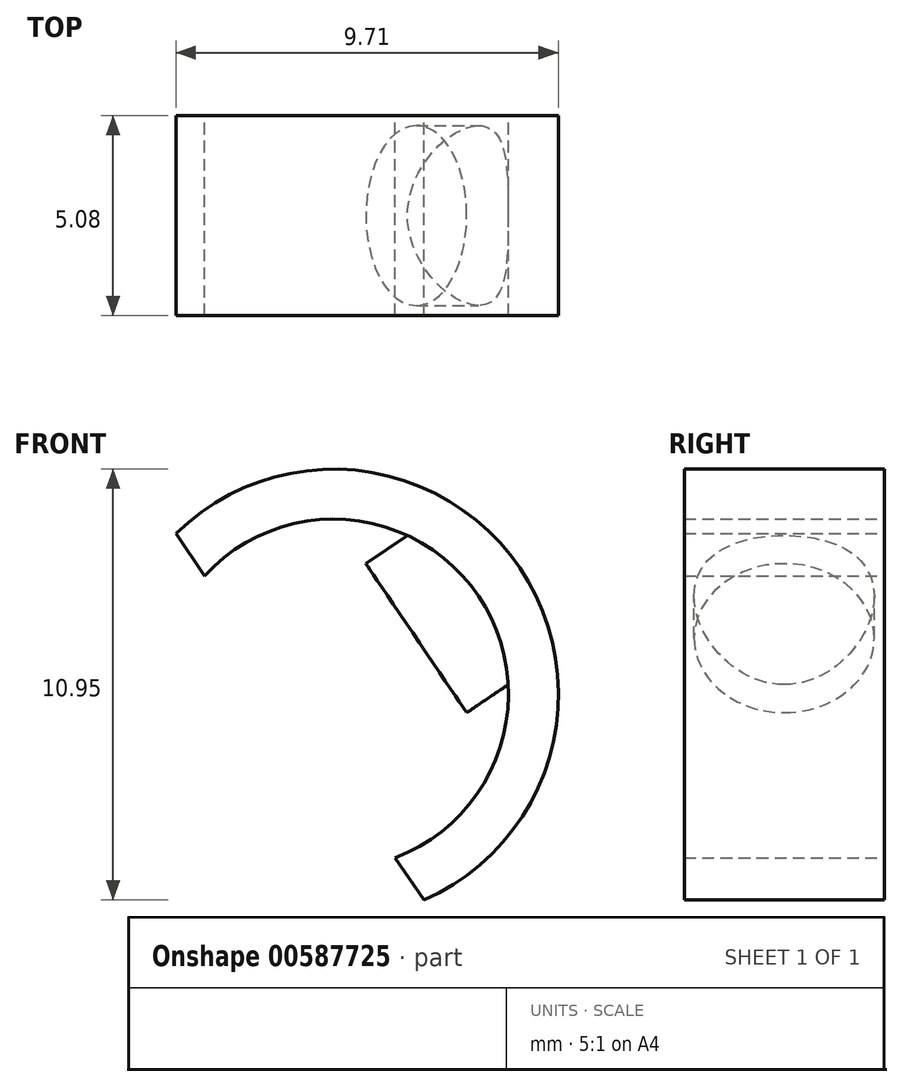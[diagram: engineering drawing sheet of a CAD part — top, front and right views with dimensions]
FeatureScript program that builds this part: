
annotation { "Feature Type Name" : "Feature", "Feature Type Description" : "" }
export const myFeature = defineFeature(function(context is Context, id is Id, definition is map)
    precondition{}
    {
        {
            var Q0;
            Q0=qCreatedBy(makeId("Front.planeOp"),FACE);
            var sketch = newSketch(context, id + "F0", { "sketchPlane" : qUnion([Q0])});
            skArc(sketch, "E0", {"start": v(1.57, -4.16) * mm, "mid": v(3.68, 2.49) * mm, "end": v(-3.28, 3) * mm});
            skArc(sketch, "E1", {"start": v(2.3, -5.23) * mm, "mid": v(4.73, 3.2) * mm, "end": v(-4, 4.08) * mm});
            skLineSegment(sketch, "E2", {"start": v(-4, 4.08) * mm, "end": v(-3.28, 3) * mm});
            skLineSegment(sketch, "E3.trimOffspring", {"start": v(1.57, -4.16) * mm, "end": v(2.3, -5.23) * mm});
            skSolve(sketch);
        }
        {
            var Q0;
            Q0 = qSketchRegion(id + "F0", true);
            extrude(context, id + "F1", {"entities" : qUnion([Q0]), "depth" : 5.08 * mm, "offsetDistance" : 25.4 * mm});
        }
        {
            var Q0;
            Q0=makeQuery(id+"F1.opExtrude","CAP_EDGE",EDGE,{"disambiguationData":[OSD([sQuery(id+"F0.wireOp",EDGE,"E0")])],"isStart":false});
            cPoint(context, id + "F2", {"entities" : qUnion([Q0]), "parameter" : 0.5});
        }
        {
            var Q0;
            Q0=makeQuery(id+"F1.opExtrude","CAP_EDGE",EDGE,{"disambiguationData":[OSD([sQuery(id+"F0.wireOp",EDGE,"E1")])],"isStart":false});
            cPoint(context, id + "F3", {"entities" : qUnion([Q0]), "parameter" : 0.5});
        }
        {
            var Q0;
            Q0 = qCreatedBy(id + "F2" ,VERTEX);
            var Q1;
            Q1 = qCreatedBy(id + "F3" ,VERTEX);
            cPlane(context, id + "F4", {"entities" : qUnion([Q0, Q1]), "cplaneType" : CPlaneType.MID_PLANE, "offset" : 25.4 * mm, "width" : 152.4 * mm, "height" : 152.4 * mm});
        }
        {
            var Q0;
            Q0=qCreatedBy(id+"F4.planeOp",FACE);
            var sketch = newSketch(context, id + "F5", { "sketchPlane" : qUnion([Q0])});
            skCircle(sketch, "E4", {"center": v(-2.54, 0) * mm, "radius": 2.29 * mm});
            skPoint(sketch, "E5", {"position": v(-2.54, 4.32) * mm});
            skSolve(sketch);
        }
        {
            var Q0;
            Q0 = qSketchRegion(id + "F5", true);
            extrude(context, id + "F6", {"entities" : qUnion([Q0]), "operationType" : NewBodyOperationType.ADD, "oppositeDirection" : true, "depth" : 2.54 * mm, "offsetDistance" : 25.4 * mm});
        }
    });
